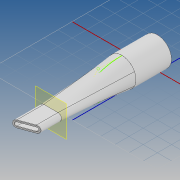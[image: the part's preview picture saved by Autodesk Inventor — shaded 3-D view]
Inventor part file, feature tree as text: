
AUTODESK INVENTOR PART (.ipt)
format: ipt  version: 2021 (Build 250183000, 183)  size: 298,496 bytes
history: native  units: mm
features: sketch x5, projected_geometry x5, extrude x4, other x4, loft x2, plane x1, fillet x1
ambient origin geometry x8: Origin, YZ Plane, XZ Plane, XY Plane, X Axis, Y Axis, Z Axis, Center Point
bodies: Solid1 (feature_tree), Solid3 (feature_tree)
feature tree (22):
  extrude  "Extrusion1"  Depth=100.0mm
  plane  "Work Plane1"
  sketch  "Sketch3"  dims[d5=10.0mm d6=10.0mm]
  extrude  "Extrusion2"  Depth=10.0mm
  sketch  "Sketch7"  dims[d19=2.5mm d22=39.65mm]
  extrude  "Extrusion5"  Depth=50.0mm TaperAngle=0.0deg
  loft  "Loft3"
  loft  "Loft5"
  extrude  "Extrusion6"  TaperAngle=0.0deg  [1 undecoded]
  fillet  "Fillet1"  [1 undecoded]
  sketch  "Sketch2"  dims[d2=50.0mm d3=0.0mm d4=100.0mm]
  projected_geometry  "Projected Loop1"
  sketch  "Sketch4"  dims[d11=34.65mm d12=50.0mm d13=0.0mm]
  projected_geometry  "Projected Loop5"
  other  "Edges4"
  other  "Edges5"
  other  "Edges8"
  other  "Edges9"
  sketch  "Sketch8"  dims[d23=40.0mm d24=0.0mm d33=0.0mm d34=90.0deg d35=0.0mm d36=90.0deg d41=0.0mm d42=90.0deg d43=0.0mm d44=90.0deg d45=3.490659mm d46=10.0mm d47=0.0mm d48=0.5mm]
  projected_geometry  "Projected Loop7"
  projected_geometry  "Projected Loop8"
  projected_geometry  "Projected Loop9"
note: 2 required parameter values undecoded (feature->parameter linkage not recoverable at this tier; creation-order binding heuristic only, values carry confidence <= 0.55)
